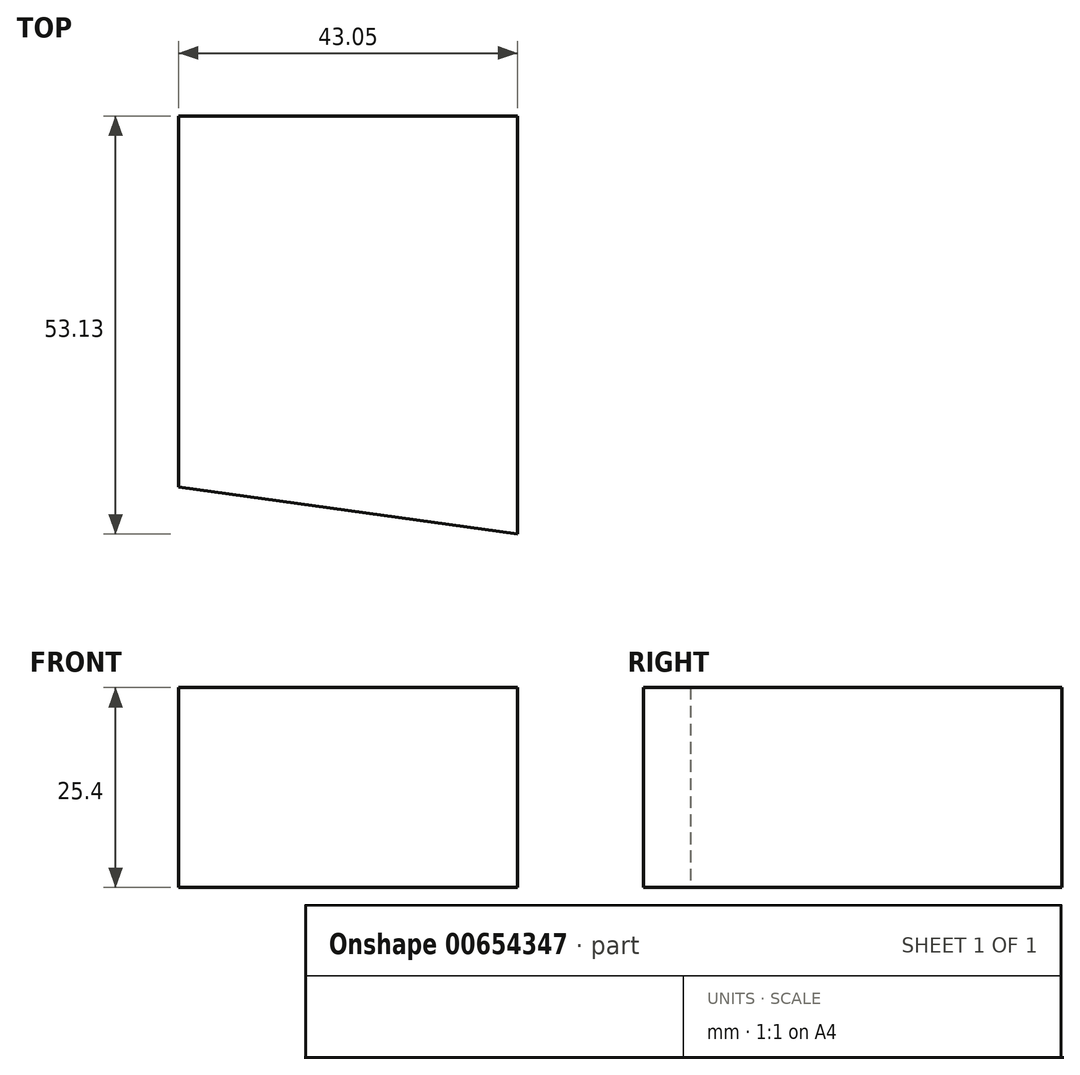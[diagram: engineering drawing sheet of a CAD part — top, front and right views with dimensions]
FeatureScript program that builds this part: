
annotation { "Feature Type Name" : "Feature", "Feature Type Description" : "" }
export const myFeature = defineFeature(function(context is Context, id is Id, definition is map)
    precondition{}
    {
        {
            var Q0;
            Q0=qCreatedBy(makeId("Top.planeOp"),FACE);
            var sketch = newSketch(context, id + "F0", { "sketchPlane" : qUnion([Q0])});
            skLineSegment(sketch, "E0", {"start": v(-61.6, -47.13) * mm, "end": v(-61.6, 0) * mm});
            skLineSegment(sketch, "E1", {"start": v(-61.6, 0) * mm, "end": v(-18.55, 0) * mm});
            skLineSegment(sketch, "E2", {"start": v(-18.55, 0) * mm, "end": v(-18.55, -53.13) * mm});
            skLineSegment(sketch, "E3", {"start": v(-18.55, -53.13) * mm, "end": v(-61.6, -47.13) * mm});
            skSolve(sketch);
        }
        {
            var Q0;
            Q0=makeQuery(id+"F0.imprint","IMPRINT",FACE,{"disambiguationData":[TD([[makeQuery(id+"F0.imprint","IMPRINT",EDGE,{"derivedFrom":sQuery(id+"F0.wireOp",EDGE,"E0")}),-1.0]])]});
            extrude(context, id + "F1", {"entities" : qUnion([Q0]), "depth" : 25.4 * mm, "offsetDistance" : 25.4 * mm});
        }
    });
